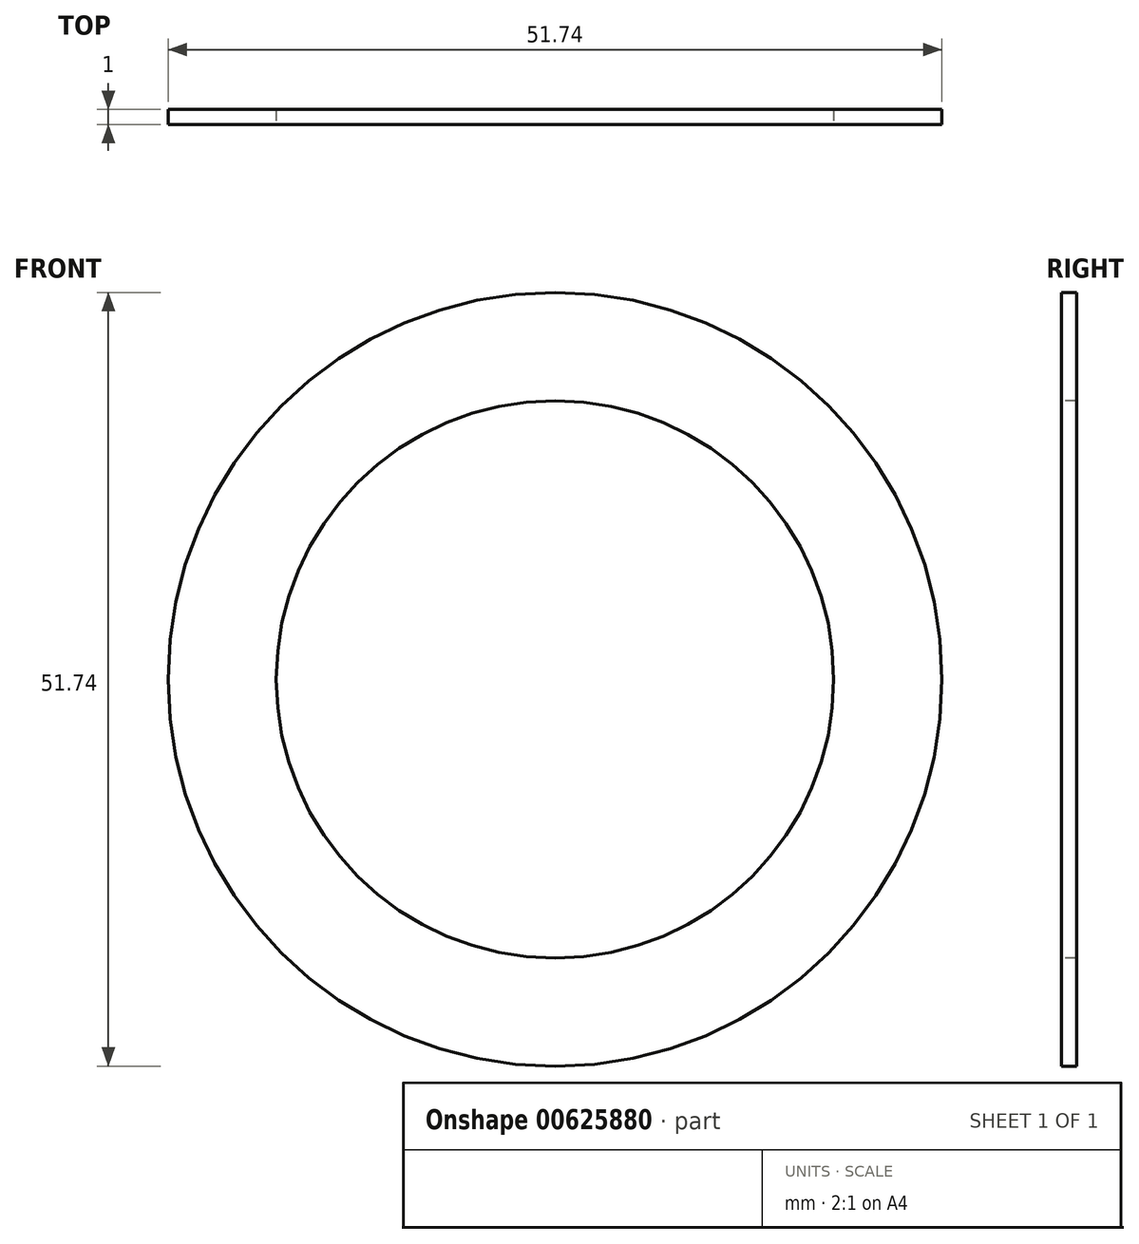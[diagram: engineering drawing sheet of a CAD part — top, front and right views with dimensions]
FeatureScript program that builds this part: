
annotation { "Feature Type Name" : "Feature", "Feature Type Description" : "" }
export const myFeature = defineFeature(function(context is Context, id is Id, definition is map)
    precondition{}
    {
        {
            var Q0;
            Q0=qCreatedBy(makeId("Front.planeOp"),FACE);
            var sketch = newSketch(context, id + "F0", { "sketchPlane" : qUnion([Q0])});
            skCircle(sketch, "E0", {"center": v(0, 0) * mm, "radius": 18.64 * mm});
            skCircle(sketch, "E1", {"center": v(0, 0) * mm, "radius": 25.87 * mm});
            skSolve(sketch);
        }
        {
            var Q0;
            Q0=sQuery(id+"F0.wireOp",EDGE,"E0");
            var Q1;
            Q1=sQuery(id+"F0.wireOp",EDGE,"E1");
            extrude(context, id + "F1", {"bodyType" : ToolBodyType.SURFACE, "surfaceEntities" : qUnion([Q0, Q1]), "depth" : 1 * mm, "offsetDistance" : 25 * mm});
        }
    });
